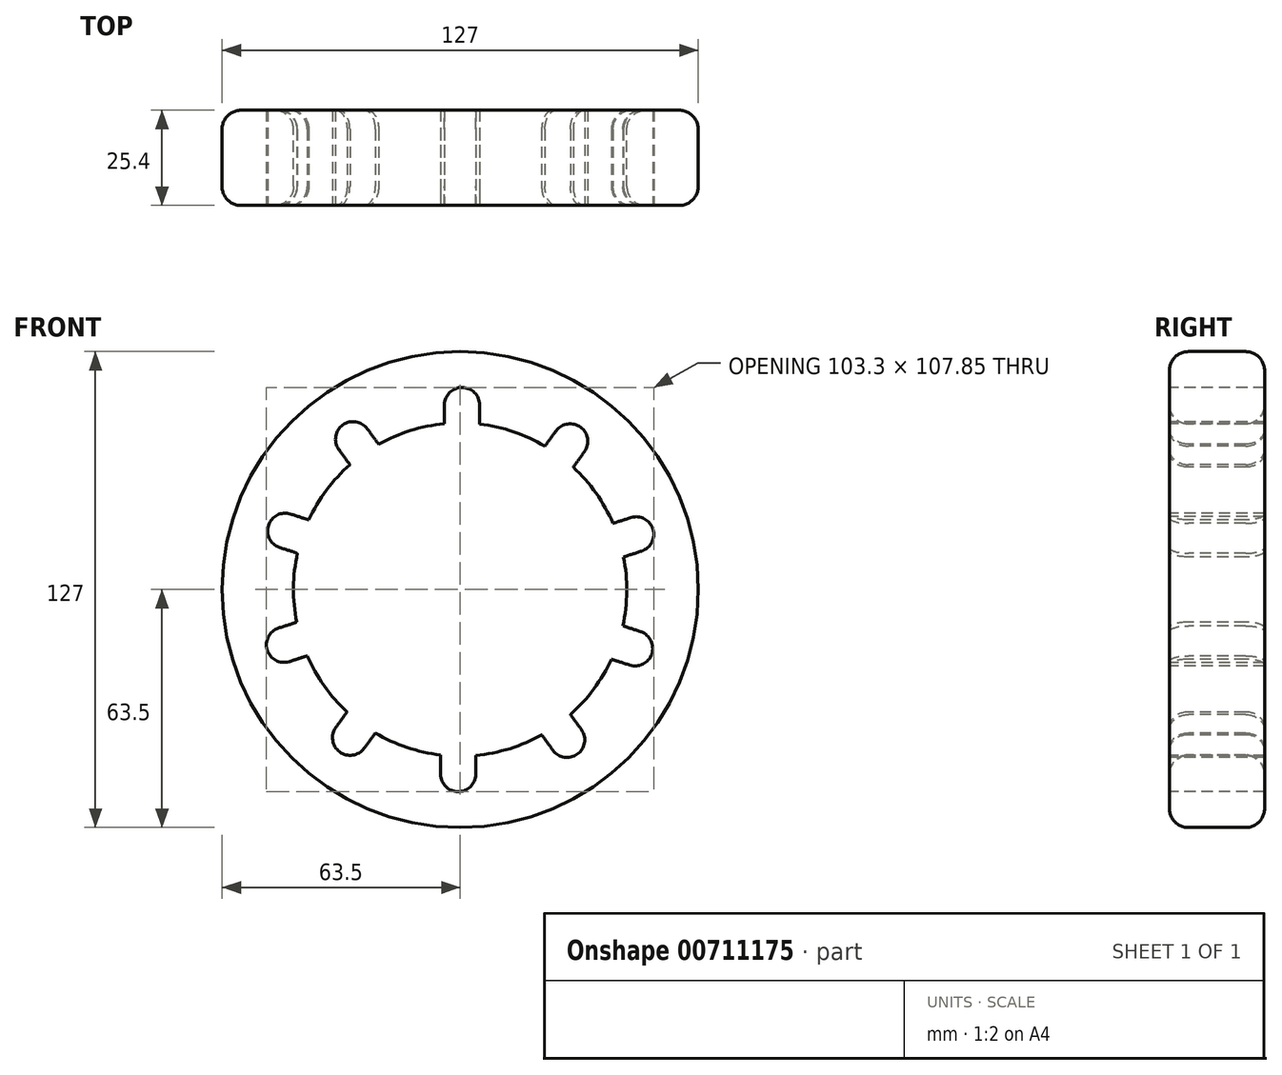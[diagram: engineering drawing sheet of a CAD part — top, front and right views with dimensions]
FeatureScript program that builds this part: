
annotation { "Feature Type Name" : "Feature", "Feature Type Description" : "" }
export const myFeature = defineFeature(function(context is Context, id is Id, definition is map)
    precondition{}
    {
        {
            var Q0;
            Q0=qCreatedBy(makeId("Front.planeOp"),FACE);
            var sketch = newSketch(context, id + "F0", { "sketchPlane" : qUnion([Q0])});
            skCircle(sketch, "E0", {"center": v(0, 0) * mm, "radius": 63.5 * mm});
            skCircle(sketch, "E1", {"center": v(0, 0) * mm, "radius": 44.45 * mm});
            skSolve(sketch);
        }
        {
            var Q0;
            Q0 = qSketchRegion(id + "F0", true);
            extrude(context, id + "F1", {"entities" : qUnion([Q0]), "depth" : 25.4 * mm, "offsetDistance" : 25.4 * mm});
        }
        {
            var Q0;
            Q0=makeQuery(id+"F1.opExtrude","CAP_FACE",FACE,{"disambiguationData":[OSD([sQuery(id+"F0.wireOp",EDGE,"E0"),sQuery(id+"F0.wireOp",EDGE,"E1")])],"isStart":false});
            var sketch = newSketch(context, id + "F2", { "sketchPlane" : qUnion([Q0])});
            skLineSegment(sketch, "E2", {"start": v(-4.2, 44.25) * mm, "end": v(-4.2, 49.23) * mm});
            skLineSegment(sketch, "E3", {"start": v(5.2, 49.23) * mm, "end": v(5.2, 44.15) * mm});
            skArc(sketch, "E4", {"start": v(5.2, 49.23) * mm, "mid": v(0.5, 53.92) * mm, "end": v(-4.2, 49.23) * mm});
            skArc(sketch, "E5.1.0", {"start": v(-24.73, 42.88) * mm, "mid": v(-31.3, 43.92) * mm, "end": v(-32.33, 37.35) * mm});
            skLineSegment(sketch, "E5.1.1", {"start": v(-29.4, 33.33) * mm, "end": v(-32.33, 37.35) * mm});
            skLineSegment(sketch, "E5.1.2", {"start": v(-24.73, 42.88) * mm, "end": v(-21.74, 38.77) * mm});
            skArc(sketch, "E5.2.0", {"start": v(-45.21, 20.15) * mm, "mid": v(-51.13, 17.14) * mm, "end": v(-48.11, 11.22) * mm});
            skLineSegment(sketch, "E5.2.1", {"start": v(-43.38, 9.68) * mm, "end": v(-48.11, 11.22) * mm});
            skLineSegment(sketch, "E5.2.2", {"start": v(-45.21, 20.15) * mm, "end": v(-40.38, 18.58) * mm});
            skArc(sketch, "E5.3.0", {"start": v(-48.42, -10.27) * mm, "mid": v(-51.44, -16.2) * mm, "end": v(-45.52, -19.2) * mm});
            skLineSegment(sketch, "E5.3.1", {"start": v(-40.79, -17.67) * mm, "end": v(-45.52, -19.2) * mm});
            skLineSegment(sketch, "E5.3.2", {"start": v(-48.42, -10.27) * mm, "end": v(-43.6, -8.7) * mm});
            skArc(sketch, "E5.4.0", {"start": v(-33.14, -36.77) * mm, "mid": v(-32.1, -43.33) * mm, "end": v(-25.53, -42.3) * mm});
            skLineSegment(sketch, "E5.4.1", {"start": v(-22.61, -38.27) * mm, "end": v(-25.53, -42.3) * mm});
            skLineSegment(sketch, "E5.4.2", {"start": v(-33.14, -36.77) * mm, "end": v(-30.15, -32.66) * mm});
            skArc(sketch, "E5.5.0", {"start": v(-5.2, -49.23) * mm, "mid": v(-0.5, -53.92) * mm, "end": v(4.2, -49.23) * mm});
            skLineSegment(sketch, "E5.5.1", {"start": v(4.2, -44.25) * mm, "end": v(4.2, -49.23) * mm});
            skLineSegment(sketch, "E5.5.2", {"start": v(-5.2, -49.23) * mm, "end": v(-5.2, -44.15) * mm});
            skArc(sketch, "E5.6.0", {"start": v(24.73, -42.88) * mm, "mid": v(31.3, -43.92) * mm, "end": v(32.33, -37.35) * mm});
            skLineSegment(sketch, "E5.6.1", {"start": v(29.4, -33.33) * mm, "end": v(32.33, -37.35) * mm});
            skLineSegment(sketch, "E5.6.2", {"start": v(24.73, -42.88) * mm, "end": v(21.74, -38.77) * mm});
            skArc(sketch, "E5.7.0", {"start": v(45.21, -20.15) * mm, "mid": v(51.13, -17.14) * mm, "end": v(48.11, -11.22) * mm});
            skLineSegment(sketch, "E5.7.1", {"start": v(43.38, -9.68) * mm, "end": v(48.11, -11.22) * mm});
            skLineSegment(sketch, "E5.7.2", {"start": v(45.21, -20.15) * mm, "end": v(40.38, -18.58) * mm});
            skArc(sketch, "E5.8.0", {"start": v(48.42, 10.27) * mm, "mid": v(51.44, 16.2) * mm, "end": v(45.52, 19.2) * mm});
            skLineSegment(sketch, "E5.8.1", {"start": v(40.79, 17.67) * mm, "end": v(45.52, 19.2) * mm});
            skLineSegment(sketch, "E5.8.2", {"start": v(48.42, 10.27) * mm, "end": v(43.6, 8.7) * mm});
            skArc(sketch, "E5.9.0", {"start": v(33.14, 36.77) * mm, "mid": v(32.1, 43.33) * mm, "end": v(25.53, 42.3) * mm});
            skLineSegment(sketch, "E5.9.1", {"start": v(22.61, 38.27) * mm, "end": v(25.53, 42.3) * mm});
            skLineSegment(sketch, "E5.9.2", {"start": v(33.14, 36.77) * mm, "end": v(30.15, 32.66) * mm});
            skPoint(sketch, "E5.center", {"position": v(0, 0) * mm});
            skSolve(sketch);
        }
        {
            var Q0;
            Q0=makeQuery(id+"F2.imprint","IMPRINT",FACE,{"disambiguationData":[TD([[makeQuery(id+"F2.imprint","IMPRINT",EDGE,{"derivedFrom":sQuery(id+"F2.wireOp",EDGE,"E5.2.0")}),1.0]])]});
            var Q1;
            Q1=makeQuery(id+"F2.imprint","IMPRINT",FACE,{"disambiguationData":[TD([[makeQuery(id+"F2.imprint","IMPRINT",EDGE,{"derivedFrom":sQuery(id+"F2.wireOp",EDGE,"E5.1.0")}),1.0]])]});
            var Q2;
            {var subQ0=sQuery(id+"F2.wireOp",EDGE,"E2");Q2=makeQuery(id+"F2.imprint","IMPRINT",FACE,{"disambiguationData":[TD([[makeQuery(id+"F2.imprint","IMPRINT",EDGE,{"derivedFrom":subQ0}),-1.0]])]});}
            var Q3;
            Q3=makeQuery(id+"F2.imprint","IMPRINT",FACE,{"disambiguationData":[TD([[makeQuery(id+"F2.imprint","IMPRINT",EDGE,{"derivedFrom":sQuery(id+"F2.wireOp",EDGE,"E5.9.0")}),1.0]])]});
            var Q4;
            Q4=makeQuery(id+"F2.imprint","IMPRINT",FACE,{"disambiguationData":[TD([[makeQuery(id+"F2.imprint","IMPRINT",EDGE,{"derivedFrom":sQuery(id+"F2.wireOp",EDGE,"E5.8.0")}),1.0]])]});
            var Q5;
            Q5=makeQuery(id+"F2.imprint","IMPRINT",FACE,{"disambiguationData":[TD([[makeQuery(id+"F2.imprint","IMPRINT",EDGE,{"derivedFrom":sQuery(id+"F2.wireOp",EDGE,"E5.7.0")}),1.0]])]});
            var Q6;
            Q6=makeQuery(id+"F2.imprint","IMPRINT",FACE,{"disambiguationData":[TD([[makeQuery(id+"F2.imprint","IMPRINT",EDGE,{"derivedFrom":sQuery(id+"F2.wireOp",EDGE,"E5.6.0")}),1.0]])]});
            var Q7;
            Q7=makeQuery(id+"F2.imprint","IMPRINT",FACE,{"disambiguationData":[TD([[makeQuery(id+"F2.imprint","IMPRINT",EDGE,{"derivedFrom":sQuery(id+"F2.wireOp",EDGE,"E5.5.0")}),1.0]])]});
            var Q8;
            Q8=makeQuery(id+"F2.imprint","IMPRINT",FACE,{"disambiguationData":[TD([[makeQuery(id+"F2.imprint","IMPRINT",EDGE,{"derivedFrom":sQuery(id+"F2.wireOp",EDGE,"E5.4.0")}),1.0]])]});
            var Q9;
            Q9=makeQuery(id+"F2.imprint","IMPRINT",FACE,{"disambiguationData":[TD([[makeQuery(id+"F2.imprint","IMPRINT",EDGE,{"derivedFrom":sQuery(id+"F2.wireOp",EDGE,"E5.3.0")}),1.0]])]});
            extrude(context, id + "F3", {"entities" : qUnion([Q0, Q1, Q2, Q3, Q4, Q5, Q6, Q7, Q8, Q9]), "operationType" : NewBodyOperationType.REMOVE, "oppositeDirection" : true, "depth" : 25.4 * mm, "offsetDistance" : 25.4 * mm});
        }
        {
            var Q0;
            {var subQ0=sQuery(id+"F0.wireOp",EDGE,"E1");Q0=makeQuery(id+"F3.boolean.opBoolean","SPLIT",EDGE,{"disambiguationData":[TD([makeQuery(id+"F3.opExtrude","SWEPT_FACE",FACE,{"disambiguationData":[OSD([sQuery(id+"F2.wireOp",EDGE,"E5.1.1")])]})])],"derivedFrom":makeQuery(id+"F1.opExtrude","CAP_EDGE",EDGE,{"disambiguationData":[OSD([subQ0])],"isStart":false})});}
            var Q1;
            {var subQ0=sQuery(id+"F0.wireOp",EDGE,"E1");Q1=makeQuery(id+"F3.boolean.opBoolean","SPLIT",EDGE,{"disambiguationData":[TD([makeQuery(id+"F3.opExtrude","SWEPT_FACE",FACE,{"disambiguationData":[OSD([sQuery(id+"F2.wireOp",EDGE,"E2")])]})])],"derivedFrom":makeQuery(id+"F1.opExtrude","CAP_EDGE",EDGE,{"disambiguationData":[OSD([subQ0])],"isStart":false})});}
            var Q2;
            {var subQ0=sQuery(id+"F0.wireOp",EDGE,"E1");Q2=makeQuery(id+"F3.boolean.opBoolean","SPLIT",EDGE,{"disambiguationData":[TD([makeQuery(id+"F3.opExtrude","SWEPT_FACE",FACE,{"disambiguationData":[OSD([sQuery(id+"F2.wireOp",EDGE,"E3")])]})])],"derivedFrom":makeQuery(id+"F1.opExtrude","CAP_EDGE",EDGE,{"disambiguationData":[OSD([subQ0])],"isStart":false})});}
            var Q3;
            {var subQ0=sQuery(id+"F0.wireOp",EDGE,"E1");Q3=makeQuery(id+"F3.boolean.opBoolean","SPLIT",EDGE,{"disambiguationData":[TD([makeQuery(id+"F3.opExtrude","SWEPT_FACE",FACE,{"disambiguationData":[OSD([sQuery(id+"F2.wireOp",EDGE,"E5.8.1")])]})])],"derivedFrom":makeQuery(id+"F1.opExtrude","CAP_EDGE",EDGE,{"disambiguationData":[OSD([subQ0])],"isStart":false})});}
            var Q4;
            {var subQ0=sQuery(id+"F0.wireOp",EDGE,"E1");Q4=makeQuery(id+"F3.boolean.opBoolean","SPLIT",EDGE,{"disambiguationData":[TD([makeQuery(id+"F3.opExtrude","SWEPT_FACE",FACE,{"disambiguationData":[OSD([sQuery(id+"F2.wireOp",EDGE,"E5.7.1")])]})])],"derivedFrom":makeQuery(id+"F1.opExtrude","CAP_EDGE",EDGE,{"disambiguationData":[OSD([subQ0])],"isStart":false})});}
            var Q5;
            {var subQ0=sQuery(id+"F0.wireOp",EDGE,"E1");Q5=makeQuery(id+"F3.boolean.opBoolean","SPLIT",EDGE,{"disambiguationData":[TD([makeQuery(id+"F3.opExtrude","SWEPT_FACE",FACE,{"disambiguationData":[OSD([sQuery(id+"F2.wireOp",EDGE,"E5.6.1")])]})])],"derivedFrom":makeQuery(id+"F1.opExtrude","CAP_EDGE",EDGE,{"disambiguationData":[OSD([subQ0])],"isStart":false})});}
            var Q6;
            {var subQ0=sQuery(id+"F0.wireOp",EDGE,"E1");Q6=makeQuery(id+"F3.boolean.opBoolean","SPLIT",EDGE,{"disambiguationData":[TD([makeQuery(id+"F3.opExtrude","SWEPT_FACE",FACE,{"disambiguationData":[OSD([sQuery(id+"F2.wireOp",EDGE,"E5.5.1")])]})])],"derivedFrom":makeQuery(id+"F1.opExtrude","CAP_EDGE",EDGE,{"disambiguationData":[OSD([subQ0])],"isStart":false})});}
            var Q7;
            {var subQ0=sQuery(id+"F0.wireOp",EDGE,"E1");Q7=makeQuery(id+"F3.boolean.opBoolean","SPLIT",EDGE,{"disambiguationData":[TD([makeQuery(id+"F3.opExtrude","SWEPT_FACE",FACE,{"disambiguationData":[OSD([sQuery(id+"F2.wireOp",EDGE,"E5.4.1")])]})])],"derivedFrom":makeQuery(id+"F1.opExtrude","CAP_EDGE",EDGE,{"disambiguationData":[OSD([subQ0])],"isStart":false})});}
            var Q8;
            {var subQ0=sQuery(id+"F0.wireOp",EDGE,"E1");Q8=makeQuery(id+"F3.boolean.opBoolean","SPLIT",EDGE,{"disambiguationData":[TD([makeQuery(id+"F3.opExtrude","SWEPT_FACE",FACE,{"disambiguationData":[OSD([sQuery(id+"F2.wireOp",EDGE,"E5.3.1")])]})])],"derivedFrom":makeQuery(id+"F1.opExtrude","CAP_EDGE",EDGE,{"disambiguationData":[OSD([subQ0])],"isStart":false})});}
            var Q9;
            {var subQ0=sQuery(id+"F0.wireOp",EDGE,"E1");Q9=makeQuery(id+"F3.boolean.opBoolean","SPLIT",EDGE,{"disambiguationData":[TD([makeQuery(id+"F3.opExtrude","SWEPT_FACE",FACE,{"disambiguationData":[OSD([sQuery(id+"F2.wireOp",EDGE,"E5.2.1")])]})])],"derivedFrom":makeQuery(id+"F1.opExtrude","CAP_EDGE",EDGE,{"disambiguationData":[OSD([subQ0])],"isStart":false})});}
            var Q10;
            {var subQ0=sQuery(id+"F0.wireOp",EDGE,"E1");Q10=makeQuery(id+"F3.boolean.opBoolean","SPLIT",EDGE,{"disambiguationData":[TD([makeQuery(id+"F3.opExtrude","SWEPT_FACE",FACE,{"disambiguationData":[OSD([sQuery(id+"F2.wireOp",EDGE,"E5.2.1")])]})])],"derivedFrom":makeQuery(id+"F1.opExtrude","CAP_EDGE",EDGE,{"disambiguationData":[OSD([subQ0])],"isStart":true})});}
            var Q11;
            {var subQ0=sQuery(id+"F0.wireOp",EDGE,"E1");Q11=makeQuery(id+"F3.boolean.opBoolean","SPLIT",EDGE,{"disambiguationData":[TD([makeQuery(id+"F3.opExtrude","SWEPT_FACE",FACE,{"disambiguationData":[OSD([sQuery(id+"F2.wireOp",EDGE,"E5.1.1")])]})])],"derivedFrom":makeQuery(id+"F1.opExtrude","CAP_EDGE",EDGE,{"disambiguationData":[OSD([subQ0])],"isStart":true})});}
            var Q12;
            {var subQ0=sQuery(id+"F0.wireOp",EDGE,"E1");Q12=makeQuery(id+"F3.boolean.opBoolean","SPLIT",EDGE,{"disambiguationData":[TD([makeQuery(id+"F3.opExtrude","SWEPT_FACE",FACE,{"disambiguationData":[OSD([sQuery(id+"F2.wireOp",EDGE,"E2")])]})])],"derivedFrom":makeQuery(id+"F1.opExtrude","CAP_EDGE",EDGE,{"disambiguationData":[OSD([subQ0])],"isStart":true})});}
            var Q13;
            {var subQ0=sQuery(id+"F0.wireOp",EDGE,"E1");Q13=makeQuery(id+"F3.boolean.opBoolean","SPLIT",EDGE,{"disambiguationData":[TD([makeQuery(id+"F3.opExtrude","SWEPT_FACE",FACE,{"disambiguationData":[OSD([sQuery(id+"F2.wireOp",EDGE,"E3")])]})])],"derivedFrom":makeQuery(id+"F1.opExtrude","CAP_EDGE",EDGE,{"disambiguationData":[OSD([subQ0])],"isStart":true})});}
            var Q14;
            {var subQ0=sQuery(id+"F0.wireOp",EDGE,"E1");Q14=makeQuery(id+"F3.boolean.opBoolean","SPLIT",EDGE,{"disambiguationData":[TD([makeQuery(id+"F3.opExtrude","SWEPT_FACE",FACE,{"disambiguationData":[OSD([sQuery(id+"F2.wireOp",EDGE,"E5.8.1")])]})])],"derivedFrom":makeQuery(id+"F1.opExtrude","CAP_EDGE",EDGE,{"disambiguationData":[OSD([subQ0])],"isStart":true})});}
            var Q15;
            {var subQ0=sQuery(id+"F0.wireOp",EDGE,"E1");Q15=makeQuery(id+"F3.boolean.opBoolean","SPLIT",EDGE,{"disambiguationData":[TD([makeQuery(id+"F3.opExtrude","SWEPT_FACE",FACE,{"disambiguationData":[OSD([sQuery(id+"F2.wireOp",EDGE,"E5.4.1")])]})])],"derivedFrom":makeQuery(id+"F1.opExtrude","CAP_EDGE",EDGE,{"disambiguationData":[OSD([subQ0])],"isStart":true})});}
            var Q16;
            {var subQ0=sQuery(id+"F0.wireOp",EDGE,"E1");Q16=makeQuery(id+"F3.boolean.opBoolean","SPLIT",EDGE,{"disambiguationData":[TD([makeQuery(id+"F3.opExtrude","SWEPT_FACE",FACE,{"disambiguationData":[OSD([sQuery(id+"F2.wireOp",EDGE,"E5.3.1")])]})])],"derivedFrom":makeQuery(id+"F1.opExtrude","CAP_EDGE",EDGE,{"disambiguationData":[OSD([subQ0])],"isStart":true})});}
            var Q17;
            {var subQ0=sQuery(id+"F0.wireOp",EDGE,"E1");Q17=makeQuery(id+"F3.boolean.opBoolean","SPLIT",EDGE,{"disambiguationData":[TD([makeQuery(id+"F3.opExtrude","SWEPT_FACE",FACE,{"disambiguationData":[OSD([sQuery(id+"F2.wireOp",EDGE,"E5.5.1")])]})])],"derivedFrom":makeQuery(id+"F1.opExtrude","CAP_EDGE",EDGE,{"disambiguationData":[OSD([subQ0])],"isStart":true})});}
            var Q18;
            {var subQ0=sQuery(id+"F0.wireOp",EDGE,"E1");Q18=makeQuery(id+"F3.boolean.opBoolean","SPLIT",EDGE,{"disambiguationData":[TD([makeQuery(id+"F3.opExtrude","SWEPT_FACE",FACE,{"disambiguationData":[OSD([sQuery(id+"F2.wireOp",EDGE,"E5.6.1")])]})])],"derivedFrom":makeQuery(id+"F1.opExtrude","CAP_EDGE",EDGE,{"disambiguationData":[OSD([subQ0])],"isStart":true})});}
            var Q19;
            {var subQ0=sQuery(id+"F0.wireOp",EDGE,"E1");Q19=makeQuery(id+"F3.boolean.opBoolean","SPLIT",EDGE,{"disambiguationData":[TD([makeQuery(id+"F3.opExtrude","SWEPT_FACE",FACE,{"disambiguationData":[OSD([sQuery(id+"F2.wireOp",EDGE,"E5.7.1")])]})])],"derivedFrom":makeQuery(id+"F1.opExtrude","CAP_EDGE",EDGE,{"disambiguationData":[OSD([subQ0])],"isStart":true})});}
            fillet(context, id + "F4", {"entities" : qUnion([Q0, Q1, Q2, Q3, Q4, Q5, Q6, Q7, Q8, Q9, Q10, Q11, Q12, Q13, Q14, Q15, Q16, Q17, Q18, Q19]), "radius" : 5.08 * mm, "tangentPropagation" : true, "allowEdgeOverflow" : false});
        }
        {
            var Q0;
            Q0=makeQuery(id+"F1.opExtrude","CAP_EDGE",EDGE,{"disambiguationData":[OSD([sQuery(id+"F0.wireOp",EDGE,"E0")])],"isStart":false});
            var Q1;
            Q1=makeQuery(id+"F1.opExtrude","CAP_EDGE",EDGE,{"disambiguationData":[OSD([sQuery(id+"F0.wireOp",EDGE,"E0")])],"isStart":true});
            fillet(context, id + "F5", {"entities" : qUnion([Q0, Q1]), "radius" : 5.08 * mm, "tangentPropagation" : true, "allowEdgeOverflow" : false});
        }
    });
